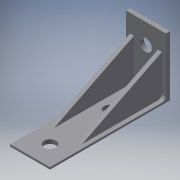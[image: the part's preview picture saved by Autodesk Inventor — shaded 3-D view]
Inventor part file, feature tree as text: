
AUTODESK INVENTOR PART (.ipt)
format: ipt  version: 2018.1 (Build 221171000, 171)  size: 167,936 bytes
history: native  units: in
note: dims shown in document units (in); Inventor stores cm internally (conversion verified against a paired STEP export)
features: sketch x6, plane x2, rib x2, hole x2, sweep x1, chamfer x1, fillet x1
ambient origin geometry x8: Origin, YZ Plane, XZ Plane, XY Plane, X Axis, Y Axis, Z Axis, Center Point
bodies: Solid1 (feature_tree)
feature tree (15):
  sweep  "Sweep1"
  plane  "Work Plane1"
  plane  "Work Plane2"
  rib  "Rib1"
  rib  "Rib2"
  chamfer  "Chamfer1"  Distance=0.7874in
  fillet  "Fillet1"  Radius=1.5748in
  hole  "Hole1"  [1 undecoded]
  hole  "Hole2"  [1 undecoded]
  sketch  "Sketch1"  dims[d0=0.7874in d1=0.0787in]
  sketch  "Sketch2"  dims[d2=2.3228in]
  sketch  "Sketch3"  dims[d3=1.1811in]
  sketch  "Sketch4"  dims[d4=0.0in]
  sketch  "Sketch5"  dims[d5=-0.1181in]
  sketch  "Sketch6"  dims[d6=-0.1181in d7=0.7874in d8=1.5748in d9=0.0394in d10=0.0787in d11=0.0in d12=0.0in d13=0.0394in d14=0.0394in d15=1.5748in d16=0.7874in d17=0.0394in d18=0.0787in d19=0.0in d20=0.0in d21=0.0394in d22=0.0394in d23=0.0394in d24=0.0787in d25=45.0deg d26=0.0787in d27=0.3937in d28=1.1811in d29=0.3937in d30=0.2362in d31=0.2362in d32=0.1575in d33=0.0787in d34=90.0deg d35=0.315in d36=0.8108in d37=0.3937in d38=0.3937in d39=0.2362in d40=0.2362in d41=0.1575in d42=0.0787in d43=90.0deg d44=0.315in d45=0.8108in d46=0.0in]
note: 2 required parameter values undecoded (feature->parameter linkage not recoverable at this tier; creation-order binding heuristic only, values carry confidence <= 0.55)
